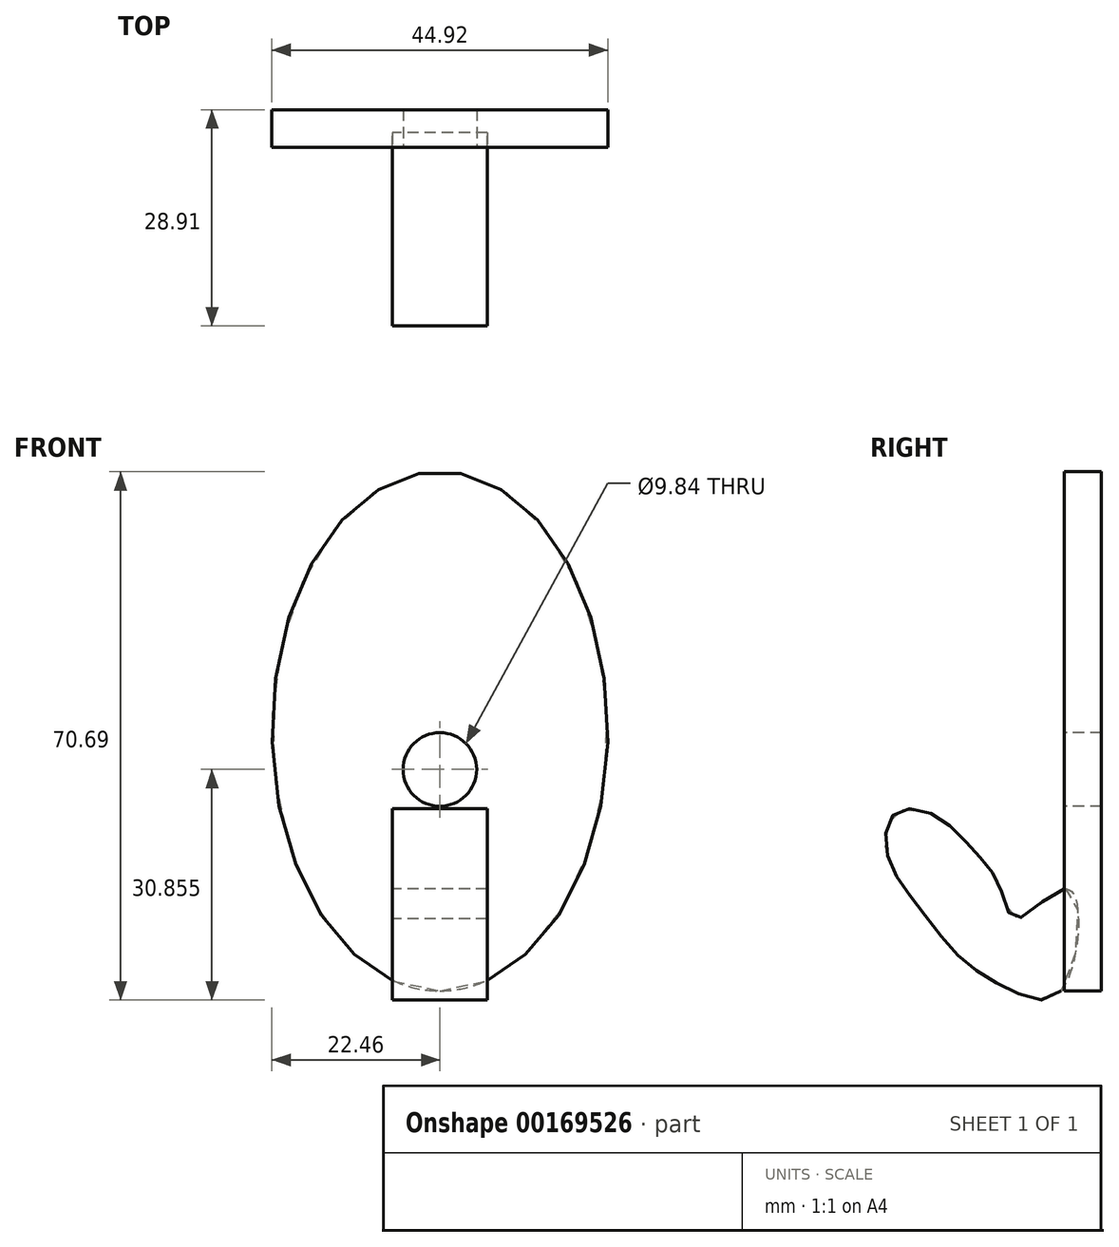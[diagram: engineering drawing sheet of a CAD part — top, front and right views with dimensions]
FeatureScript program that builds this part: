
annotation { "Feature Type Name" : "Feature", "Feature Type Description" : "" }
export const myFeature = defineFeature(function(context is Context, id is Id, definition is map)
    precondition{}
    {
        {
            var Q0;
            Q0=qCreatedBy(makeId("Front.planeOp"),FACE);
            var sketch = newSketch(context, id + "F0", { "sketchPlane" : qUnion([Q0])});
            skEllipse(sketch, "E0", {"center": v(0, 34.72) * mm, "majorRadius": 34.72 * mm, "minorRadius": 22.46 * mm, "majorAxis": v(0, -1)});
            skSolve(sketch);
        }
        {
            var Q0;
            Q0=makeQuery(id+"F0.imprint","IMPRINT",FACE,{"disambiguationData":[TD([[makeQuery(id+"F0.imprint","IMPRINT",EDGE,{"derivedFrom":sQuery(id+"F0.wireOp",EDGE,"E0")}),1.0]])]});
            extrude(context, id + "F1", {"entities" : qUnion([Q0]), "depth" : 5 * mm});
        }
        {
            var Q0;
            Q0=makeQuery(id+"F1.opExtrude","CAP_FACE",FACE,{"disambiguationData":[OSD([sQuery(id+"F0.wireOp",EDGE,"E0")])],"isStart":false});
            var sketch = newSketch(context, id + "F2", { "sketchPlane" : qUnion([Q0])});
            skCircle(sketch, "E1", {"center": v(0, 29.62) * mm, "radius": 4.92 * mm});
            skSolve(sketch);
        }
        {
            var Q0;
            Q0=makeQuery(id+"F2.imprint","IMPRINT",FACE,{"disambiguationData":[TD([[makeQuery(id+"F2.imprint","IMPRINT",EDGE,{"derivedFrom":sQuery(id+"F2.wireOp",EDGE,"E1")}),1.0]])]});
            extrude(context, id + "F3", {"entities" : qUnion([Q0]), "operationType" : NewBodyOperationType.REMOVE, "oppositeDirection" : true, "depth" : 28.25 * mm});
        }
        {
            var Q0;
            Q0=qCreatedBy(makeId("Right.planeOp"),FACE);
            var sketch = newSketch(context, id + "F4", { "sketchPlane" : qUnion([Q0])});
            skFitSpline(sketch, "E2", {"points": [v(-5.4, 0) * mm, v(-11.94, 0) * mm, v(-18.82, 4.42) * mm, v(-24.7, 11.62) * mm, v(-28.63, 18.16) * mm, v(-27.65, 23.72) * mm, v(-22.09, 23.4) * mm, v(-16.85, 18.49) * mm, v(-13.58, 13.9) * mm, v(-11.29, 9.65) * mm, v(-4.42, 13.58) * mm, v(-5.4, 0) * mm]});
            skSolve(sketch);
        }
        {
            var Q0;
            Q0=makeQuery(id+"F4.imprint","IMPRINT",FACE,{"disambiguationData":[TD([[makeQuery(id+"F4.imprint","IMPRINT",EDGE,{"derivedFrom":sQuery(id+"F4.wireOp",EDGE,"E2")}),-1.0]])]});
            extrude(context, id + "F5", {"entities" : qUnion([Q0]), "endBound" : BoundingType.SYMMETRIC, "depth" : 12.7 * mm});
        }
    });
